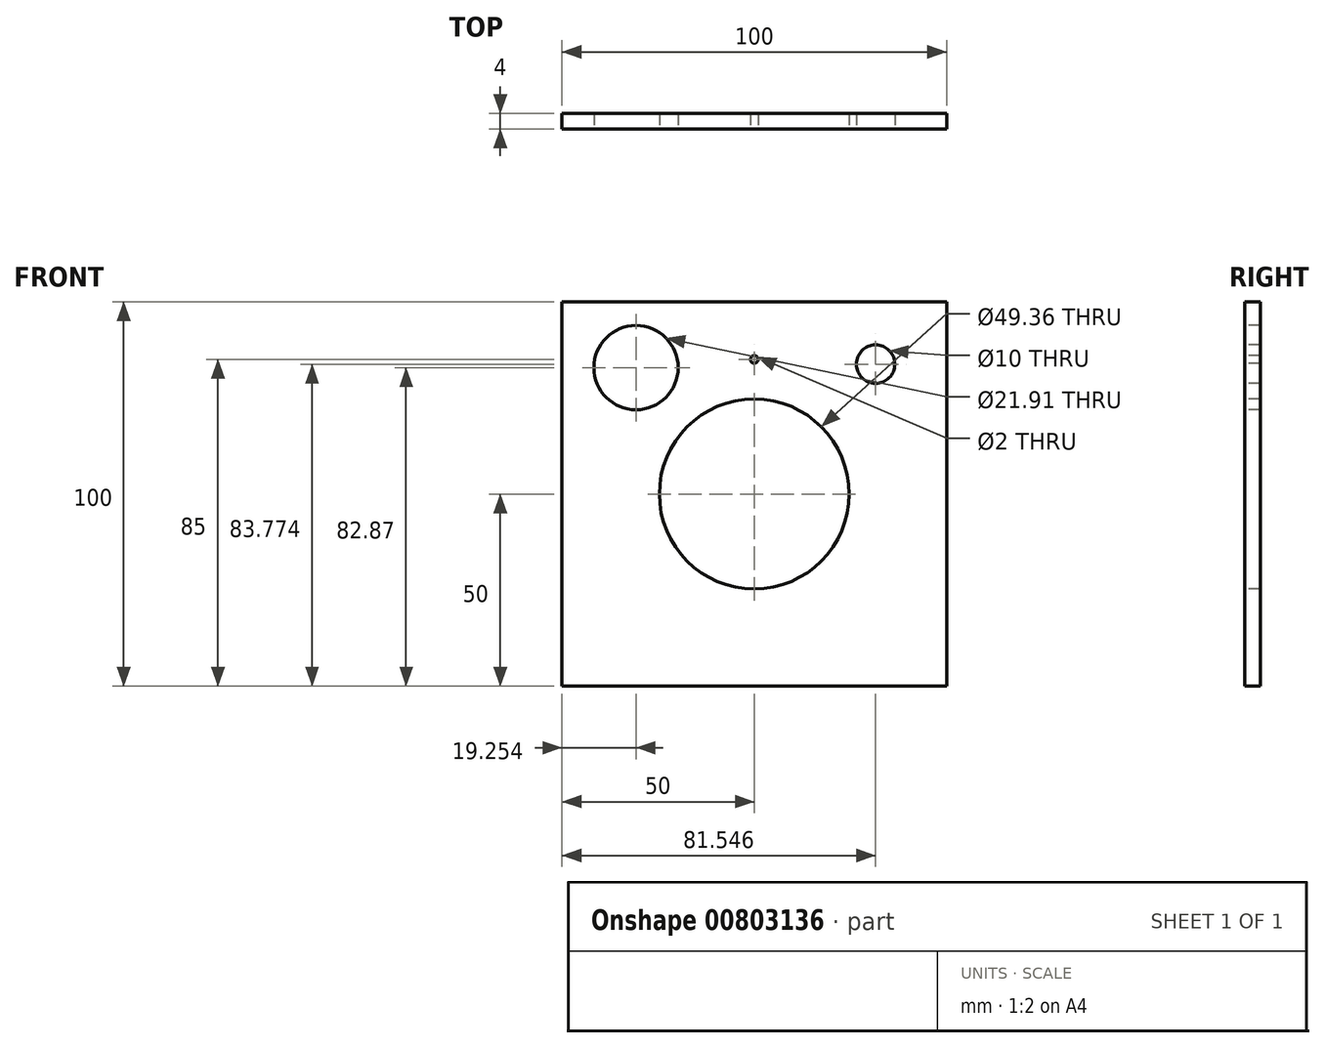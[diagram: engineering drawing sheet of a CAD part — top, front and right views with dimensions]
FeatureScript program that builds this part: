
annotation { "Feature Type Name" : "Feature", "Feature Type Description" : "" }
export const myFeature = defineFeature(function(context is Context, id is Id, definition is map)
    precondition{}
    {
        {
            var Q0;
            Q0=qCreatedBy(makeId("Front.planeOp"),FACE);
            var sketch = newSketch(context, id + "F0", { "sketchPlane" : qUnion([Q0])});
            skLineSegment(sketch, "E0.bottom", {"start": v(50, -50) * mm, "end": v(-50, -50) * mm});
            skLineSegment(sketch, "E0.top", {"start": v(50, 50) * mm, "end": v(-50, 50) * mm});
            skLineSegment(sketch, "E0.left", {"start": v(50, -50) * mm, "end": v(50, 50) * mm});
            skLineSegment(sketch, "E0.right", {"start": v(-50, -50) * mm, "end": v(-50, 50) * mm});
            skPoint(sketch, "E0.middle", {"position": v(0, 0) * mm});
            skSolve(sketch);
        }
        {
            var Q0;
            Q0 = qSketchRegion(id + "F0", true);
            extrude(context, id + "F1", {"entities" : qUnion([Q0]), "depth" : 4 * mm, "offsetDistance" : 25 * mm});
        }
        {
            var Q0;
            Q0=makeQuery(id+"F1.opExtrude","CAP_FACE",FACE,{"disambiguationData":[OSD([sQuery(id+"F0.wireOp",EDGE,"E0.bottom"),sQuery(id+"F0.wireOp",EDGE,"E0.top"),sQuery(id+"F0.wireOp",EDGE,"E0.left"),sQuery(id+"F0.wireOp",EDGE,"E0.right")])],"isStart":false});
            var sketch = newSketch(context, id + "F2", { "sketchPlane" : qUnion([Q0])});
            skCircle(sketch, "E1", {"center": v(0, 0) * mm, "radius": 24.68 * mm});
            skSolve(sketch);
        }
        {
            var Q0;
            Q0 = qSketchRegion(id + "F2", true);
            extrude(context, id + "F3", {"entities" : qUnion([Q0]), "operationType" : NewBodyOperationType.REMOVE, "oppositeDirection" : true, "depth" : 25 * mm, "offsetDistance" : 25 * mm});
        }
        {
            var Q0;
            Q0=makeQuery(id+"F1.opExtrude","CAP_FACE",FACE,{"disambiguationData":[OSD([sQuery(id+"F0.wireOp",EDGE,"E0.bottom"),sQuery(id+"F0.wireOp",EDGE,"E0.top"),sQuery(id+"F0.wireOp",EDGE,"E0.left"),sQuery(id+"F0.wireOp",EDGE,"E0.right")])],"isStart":false});
            var sketch = newSketch(context, id + "F4", { "sketchPlane" : qUnion([Q0])});
            skCircle(sketch, "E2", {"center": v(31.55, 33.77) * mm, "radius": 5 * mm});
            skSolve(sketch);
        }
        {
            var Q0;
            Q0 = qSketchRegion(id + "F4", true);
            extrude(context, id + "F5", {"entities" : qUnion([Q0]), "operationType" : NewBodyOperationType.REMOVE, "oppositeDirection" : true, "depth" : 25 * mm, "offsetDistance" : 25 * mm});
        }
        {
            var Q0;
            Q0=makeQuery(id+"F1.opExtrude","CAP_FACE",FACE,{"disambiguationData":[OSD([sQuery(id+"F0.wireOp",EDGE,"E0.bottom"),sQuery(id+"F0.wireOp",EDGE,"E0.top"),sQuery(id+"F0.wireOp",EDGE,"E0.left"),sQuery(id+"F0.wireOp",EDGE,"E0.right")])],"isStart":false});
            var sketch = newSketch(context, id + "F6", { "sketchPlane" : qUnion([Q0])});
            skCircle(sketch, "E3", {"center": v(-30.75, 32.87) * mm, "radius": 10.96 * mm});
            skSolve(sketch);
        }
        {
            var Q0;
            Q0=makeQuery(id+"F6.imprint","IMPRINT",FACE,{"disambiguationData":[TD([[makeQuery(id+"F6.imprint","IMPRINT",EDGE,{"derivedFrom":sQuery(id+"F6.wireOp",EDGE,"E3")}),1.0]])]});
            extrude(context, id + "F7", {"entities" : qUnion([Q0]), "operationType" : NewBodyOperationType.REMOVE, "oppositeDirection" : true, "depth" : 25 * mm, "offsetDistance" : 25 * mm});
        }
        {
            var Q0;
            Q0=makeQuery(id+"F1.opExtrude","CAP_FACE",FACE,{"disambiguationData":[OSD([sQuery(id+"F0.wireOp",EDGE,"E0.bottom"),sQuery(id+"F0.wireOp",EDGE,"E0.top"),sQuery(id+"F0.wireOp",EDGE,"E0.left"),sQuery(id+"F0.wireOp",EDGE,"E0.right")])],"isStart":false});
            var sketch = newSketch(context, id + "F8", { "sketchPlane" : qUnion([Q0])});
            skLineSegment(sketch, "E4", {"start": v(0, 35) * mm, "end": v(0, 0) * mm, "construction": true});
            skCircle(sketch, "E5", {"center": v(0, 35) * mm, "radius": 1 * mm});
            skSolve(sketch);
        }
        {
            var Q0;
            Q0 = qSketchRegion(id + "F8", true);
            extrude(context, id + "F9", {"entities" : qUnion([Q0]), "operationType" : NewBodyOperationType.REMOVE, "endBound" : BoundingType.THROUGH_ALL, "oppositeDirection" : true, "depth" : 25 * mm, "offsetDistance" : 25 * mm});
        }
    });
